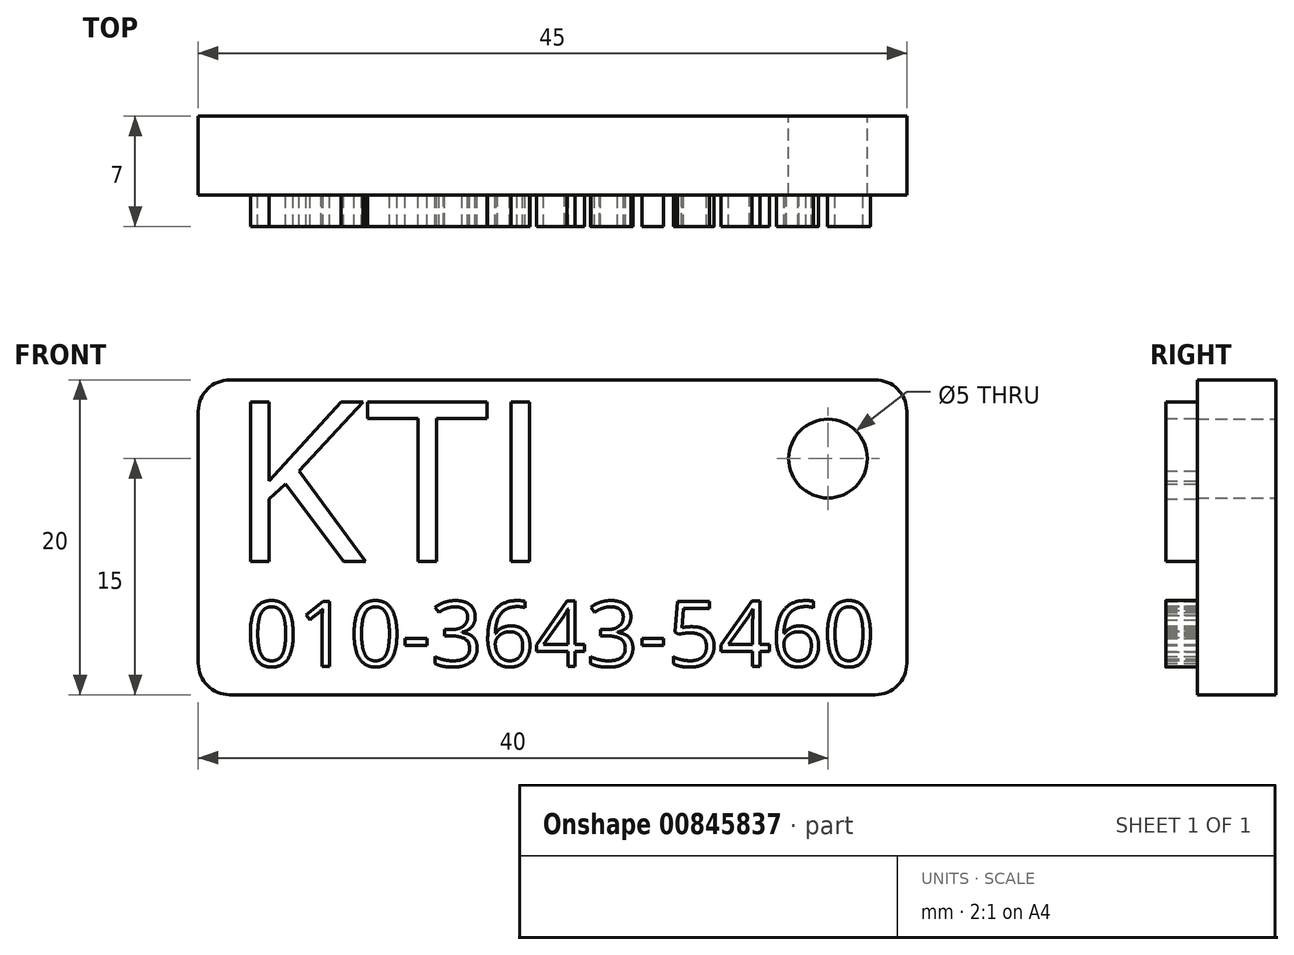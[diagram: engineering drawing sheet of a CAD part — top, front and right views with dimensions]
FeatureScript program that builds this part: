
annotation { "Feature Type Name" : "Feature", "Feature Type Description" : "" }
export const myFeature = defineFeature(function(context is Context, id is Id, definition is map)
    precondition{}
    {
        {
            var Q0;
            Q0=qCreatedBy(makeId("Front.planeOp"),FACE);
            var sketch = newSketch(context, id + "F0", { "sketchPlane" : qUnion([Q0])});
            skLineSegment(sketch, "E0.bottom", {"start": v(0, 0) * mm, "end": v(45, 0) * mm});
            skLineSegment(sketch, "E0.top", {"start": v(0, 20) * mm, "end": v(45, 20) * mm});
            skLineSegment(sketch, "E0.left", {"start": v(0, 0) * mm, "end": v(0, 20) * mm});
            skLineSegment(sketch, "E0.right", {"start": v(45, 0) * mm, "end": v(45, 20) * mm});
            skCircle(sketch, "E1", {"center": v(40, 15) * mm, "radius": 2.5 * mm});
            skPoint(sketch, "E1.first.point", {"position": v(38.59, 17.06) * mm});
            skPoint(sketch, "E1.second.point", {"position": v(42.21, 13.84) * mm});
            skPoint(sketch, "E1.third.point", {"position": v(38.45, 13.03) * mm});
            skSolve(sketch);
        }
        {
            var Q0;
            Q0=makeQuery(id+"F0.imprint","IMPRINT",FACE,{"disambiguationData":[TD([[makeQuery(id+"F0.imprint","IMPRINT",EDGE,{"derivedFrom":sQuery(id+"F0.wireOp",EDGE,"E0.bottom")}),1.0]])]});
            extrude(context, id + "F1", {"entities" : qUnion([Q0]), "depth" : 5 * mm, "offsetDistance" : 25 * mm});
        }
        {
            var Q0;
            Q0=makeQuery(id+"F1.opExtrude","CAP_FACE",FACE,{"disambiguationData":[OSD([sQuery(id+"F0.wireOp",EDGE,"E0.bottom"),sQuery(id+"F0.wireOp",EDGE,"E0.top"),sQuery(id+"F0.wireOp",EDGE,"E0.left"),sQuery(id+"F0.wireOp",EDGE,"E0.right")])],"isStart":false});
            var sketch = newSketch(context, id + "F2", { "sketchPlane" : qUnion([Q0])});
            skText(sketch, "E2", { "text": "KTI", "fontName": "OpenSans-Regular.ttf"});
            const initialGuessF2  = {"E2": [0.00193, 0.00848, 1, 0, 0.0102]};
            skSetInitialGuess(sketch, initialGuessF2);
            skSolve(sketch);
        }
        {
            var Q0;
            Q0 = qSketchRegion(id + "F2", true);
            extrude(context, id + "F3", {"entities" : qUnion([Q0]), "operationType" : NewBodyOperationType.ADD, "depth" : 2 * mm, "offsetDistance" : 25 * mm});
        }
        {
            var Q0;
            Q0=makeQuery(id+"F1.opExtrude","SWEPT_EDGE",EDGE,{"disambiguationData":[OSD([sQuery(id+"F0.wireOp",EDGE,"E0.top"),sQuery(id+"F0.wireOp",EDGE,"E0.right")])]});
            var Q1;
            Q1=makeQuery(id+"F1.opExtrude","SWEPT_EDGE",EDGE,{"disambiguationData":[OSD([sQuery(id+"F0.wireOp",EDGE,"E0.top"),sQuery(id+"F0.wireOp",EDGE,"E0.left")])]});
            var Q2;
            Q2=makeQuery(id+"F1.opExtrude","SWEPT_EDGE",EDGE,{"disambiguationData":[OSD([sQuery(id+"F0.wireOp",EDGE,"E0.bottom"),sQuery(id+"F0.wireOp",EDGE,"E0.right")])]});
            var Q3;
            Q3=makeQuery(id+"F1.opExtrude","SWEPT_EDGE",EDGE,{"disambiguationData":[OSD([sQuery(id+"F0.wireOp",EDGE,"E0.bottom"),sQuery(id+"F0.wireOp",EDGE,"E0.left")])]});
            fillet(context, id + "F4", {"entities" : qUnion([Q0, Q1, Q2, Q3]), "radius" : 2 * mm, "tangentPropagation" : true, "allowEdgeOverflow" : false});
        }
        {
            var Q0;
            Q0=makeQuery(id+"F1.opExtrude","CAP_FACE",FACE,{"disambiguationData":[OSD([sQuery(id+"F0.wireOp",EDGE,"E0.bottom"),sQuery(id+"F0.wireOp",EDGE,"E0.top"),sQuery(id+"F0.wireOp",EDGE,"E0.left"),sQuery(id+"F0.wireOp",EDGE,"E0.right"),sQuery(id+"F0.wireOp",EDGE,"E1")])],"isStart":false});
            var sketch = newSketch(context, id + "F5", { "sketchPlane" : qUnion([Q0])});
            skText(sketch, "E3", { "text": "010-3643-5460", "fontName": "OpenSans-Regular.ttf"});
            const initialGuessF5  = {"E3": [0.00302, 0.00181, 1, 0, 0.00415]};
            skSetInitialGuess(sketch, initialGuessF5);
            skSolve(sketch);
        }
        {
            var Q0;
            Q0 = qSketchRegion(id + "F5", true);
            extrude(context, id + "F6", {"entities" : qUnion([Q0]), "operationType" : NewBodyOperationType.ADD, "depth" : 2 * mm, "offsetDistance" : 25 * mm});
        }
    });
